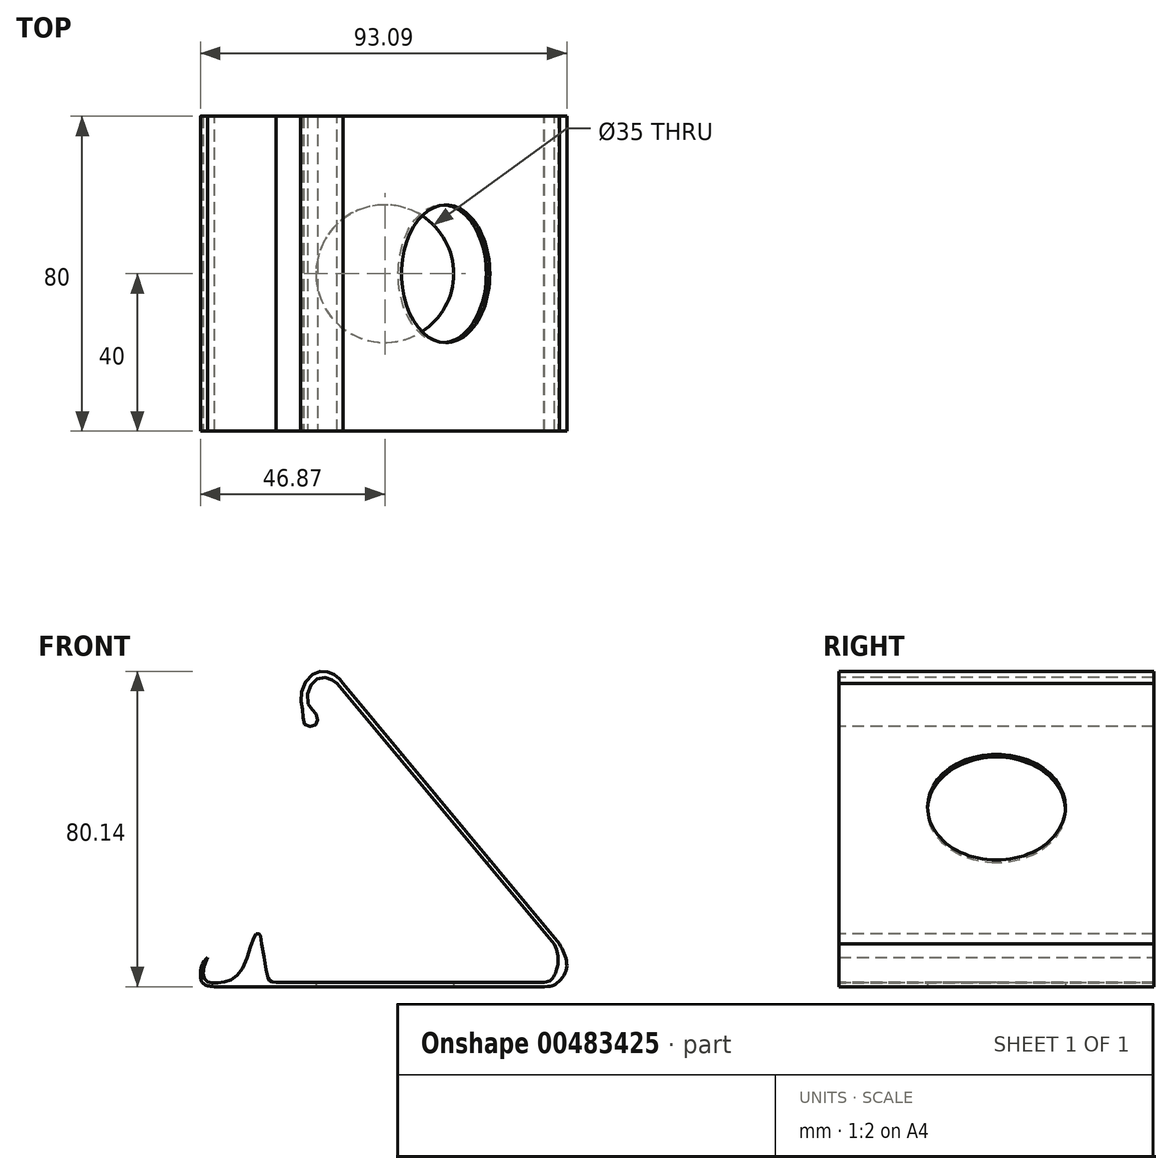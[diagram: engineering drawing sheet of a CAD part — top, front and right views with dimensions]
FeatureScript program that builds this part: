
annotation { "Feature Type Name" : "Feature", "Feature Type Description" : "" }
export const myFeature = defineFeature(function(context is Context, id is Id, definition is map)
    precondition{}
    {
        {
            var Q0;
            Q0=qCreatedBy(makeId("Front.planeOp"),FACE);
            var sketch = newSketch(context, id + "F0", { "sketchPlane" : qUnion([Q0])});
            skLineSegment(sketch, "E0", {"start": v(-43.3, -32.76) * mm, "end": v(40.56, -32.76) * mm});
            skFitSpline(sketch, "E1", {"points": [v(40.56, -32.76) * mm, v(43.39, -32.11) * mm, v(45.77, -29.3) * mm, v(46.05, -25.71) * mm, v(44.35, -21.86) * mm], "startDerivative": vector(18.76, 1.05) * mm, "endDerivative": vector(-7.5, 13.9) * mm});
            skFitSpline(sketch, "E2", {"points": [v(-43.3, -32.76) * mm, v(-46.04, -32.03) * mm, v(-46.8, -30.57) * mm, v(-45.07, -25.27) * mm], "startDerivative": vector(-11.2, 0.17) * mm, "endDerivative": vector(12.4, 12.2) * mm});
            skFitSpline(sketch, "E3", {"points": [v(-45.07, -25.27) * mm, v(-46.03, -30.3) * mm, v(-45.07, -31.56) * mm, v(-43.3, -31.87) * mm, v(-39.63, -31.24) * mm, v(-36, -27.77) * mm, v(-32.97, -19.64) * mm, v(-32.4, -19.36) * mm, v(-31.78, -19.4) * mm, v(-31.53, -20.08) * mm, v(-29.72, -30.4) * mm, v(-29.34, -31.09) * mm, v(-28.75, -31.52) * mm, v(-27.64, -31.62) * mm], "startDerivative": vector(-27.29, -58.7) * mm, "endDerivative": vector(25.46, -0.54) * mm});
            skLineSegment(sketch, "E4", {"start": v(-27.64, -31.62) * mm, "end": v(40.5, -31.62) * mm});
            skFitSpline(sketch, "E5", {"points": [v(40.5, -31.62) * mm, v(42.76, -30.44) * mm, v(43.8, -27.85) * mm, v(44.04, -25.8) * mm, v(43.04, -22.07) * mm], "startDerivative": vector(13.27, 0.53) * mm, "endDerivative": vector(-8.12, 13.57) * mm});
            skLineSegment(sketch, "E6", {"start": v(43.04, -22.07) * mm, "end": v(-12.1, 44.25) * mm});
            skLineSegment(sketch, "E7", {"start": v(44.35, -21.86) * mm, "end": v(-10.62, 44.25) * mm});
            skFitSpline(sketch, "E8", {"points": [v(-12.1, 44.25) * mm, v(-13.96, 45.45) * mm, v(-16.78, 45.65) * mm, v(-19.3, 42.8) * mm, v(-19.23, 38.53) * mm, v(-17.88, 37.03) * mm, v(-17.06, 35.34) * mm, v(-17.4, 33.91) * mm, v(-18.9, 33.3) * mm, v(-20.52, 34.11) * mm, v(-20.73, 36.9) * mm, v(-21.4, 40.21) * mm, v(-19.72, 45.33) * mm, v(-16.36, 47.33) * mm, v(-13.85, 47.01) * mm, v(-11.7, 45.66) * mm, v(-10.62, 44.25) * mm], "startDerivative": vector(-29.2, 23.65) * mm, "endDerivative": vector(18.42, -28.93) * mm});
            skSolve(sketch);
        }
        {
            var Q0;
            Q0 = qSketchRegion(id + "F0", true);
            extrude(context, id + "F1", {"entities" : qUnion([Q0]), "endBound" : BoundingType.SYMMETRIC, "depth" : 80 * mm});
        }
        {
            var Q0;
            Q0=makeQuery(id+"F1.opExtrude","SWEPT_FACE",FACE,{"disambiguationData":[OSD([sQuery(id+"F0.wireOp",EDGE,"E7")])]});
            var sketch = newSketch(context, id + "F2", { "sketchPlane" : qUnion([Q0])});
            skCircle(sketch, "E9", {"center": v(0, 0) * mm, "radius": 17.5 * mm});
            skSolve(sketch);
        }
        {
            var Q0;
            Q0 = qSketchRegion(id + "F2", true);
            extrude(context, id + "F3", {"entities" : qUnion([Q0]), "oppositeDirection" : true, "depth" : 10 * mm});
        }
        {
            var Q0;
            Q0=makeQuery(id+"F3.opExtrude","SWEPT_BODY",BODY,{"disambiguationData":[OSD([sQuery(id+"F2.wireOp",EDGE,"E9")])]});
            var Q1;
            Q1=makeQuery(id+"F1.opExtrude","SWEPT_BODY",BODY,{"disambiguationData":[OSD([sQuery(id+"F0.wireOp",EDGE,"E0"),sQuery(id+"F0.wireOp",EDGE,"E1"),sQuery(id+"F0.wireOp",EDGE,"E2"),sQuery(id+"F0.wireOp",EDGE,"E3"),sQuery(id+"F0.wireOp",EDGE,"E4"),sQuery(id+"F0.wireOp",EDGE,"E5"),sQuery(id+"F0.wireOp",EDGE,"E6"),sQuery(id+"F0.wireOp",EDGE,"E7"),sQuery(id+"F0.wireOp",EDGE,"E8")])]});
            booleanBodies(context, id + "F4", {"operationType" : BooleanOperationType.SUBTRACTION, "tools" : qUnion([Q0]), "targets" : qUnion([Q1])});
        }
        {
            var Q0;
            Q0=makeQuery(id+"F1.opExtrude","SWEPT_FACE",FACE,{"disambiguationData":[OSD([sQuery(id+"F0.wireOp",EDGE,"E0")])]});
            var sketch = newSketch(context, id + "F5", { "sketchPlane" : qUnion([Q0])});
            skCircle(sketch, "E10", {"center": v(0, 0) * mm, "radius": 17.5 * mm});
            skSolve(sketch);
        }
        {
            var Q0;
            Q0 = qSketchRegion(id + "F5", true);
            extrude(context, id + "F6", {"entities" : qUnion([Q0]), "oppositeDirection" : true, "depth" : 10 * mm});
        }
        {
            var Q0;
            Q0=makeQuery(id+"F6.opExtrude","SWEPT_BODY",BODY,{"disambiguationData":[OSD([sQuery(id+"F5.wireOp",EDGE,"E10")])]});
            var Q1;
            Q1=makeQuery(id+"F1.opExtrude","SWEPT_BODY",BODY,{"disambiguationData":[OSD([sQuery(id+"F0.wireOp",EDGE,"E0"),sQuery(id+"F0.wireOp",EDGE,"E1"),sQuery(id+"F0.wireOp",EDGE,"E2"),sQuery(id+"F0.wireOp",EDGE,"E3"),sQuery(id+"F0.wireOp",EDGE,"E4"),sQuery(id+"F0.wireOp",EDGE,"E5"),sQuery(id+"F0.wireOp",EDGE,"E6"),sQuery(id+"F0.wireOp",EDGE,"E7"),sQuery(id+"F0.wireOp",EDGE,"E8")])]});
            booleanBodies(context, id + "F7", {"operationType" : BooleanOperationType.SUBTRACTION, "tools" : qUnion([Q0]), "targets" : qUnion([Q1])});
        }
    });
